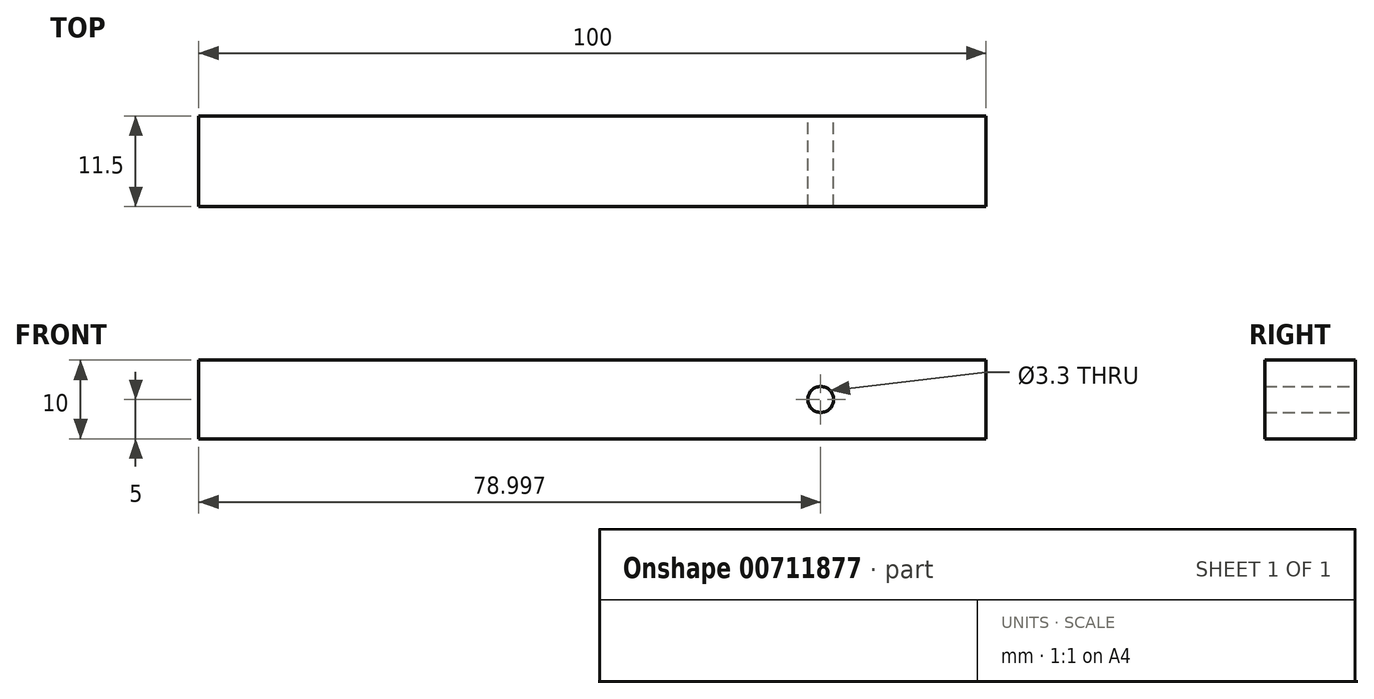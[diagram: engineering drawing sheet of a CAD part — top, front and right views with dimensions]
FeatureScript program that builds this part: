
annotation { "Feature Type Name" : "Feature", "Feature Type Description" : "" }
export const myFeature = defineFeature(function(context is Context, id is Id, definition is map)
    precondition{}
    {
        {
            var Q0;
            Q0=qCreatedBy(makeId("Top.planeOp"),FACE);
            var sketch = newSketch(context, id + "F0", { "sketchPlane" : qUnion([Q0])});
            skLineSegment(sketch, "E0.bottom", {"start": v(-19.05, 11.36) * mm, "end": v(80.95, 11.36) * mm});
            skLineSegment(sketch, "E0.top", {"start": v(-19.05, -0.14) * mm, "end": v(80.95, -0.14) * mm});
            skLineSegment(sketch, "E0.left", {"start": v(-19.05, 11.36) * mm, "end": v(-19.05, -0.14) * mm});
            skLineSegment(sketch, "E0.right", {"start": v(80.95, 11.36) * mm, "end": v(80.95, -0.14) * mm});
            skSolve(sketch);
        }
        {
            var Q0;
            Q0 = qSketchRegion(id + "F0", true);
            extrude(context, id + "F1", {"entities" : qUnion([Q0]), "depth" : 10 * mm, "offsetDistance" : 25 * mm});
        }
        {
            var Q0;
            Q0=makeQuery(id+"F1.opExtrude","SWEPT_FACE",FACE,{"disambiguationData":[OSD([sQuery(id+"F0.wireOp",EDGE,"E0.bottom")])]});
            var sketch = newSketch(context, id + "F2", { "sketchPlane" : qUnion([Q0])});
            skCircle(sketch, "E1", {"center": v(-59.95, 5) * mm, "radius": 1.65 * mm});
            skSolve(sketch);
        }
        {
            var Q0;
            Q0 = qSketchRegion(id + "F2", true);
            extrude(context, id + "F3", {"entities" : qUnion([Q0]), "operationType" : NewBodyOperationType.REMOVE, "oppositeDirection" : true, "depth" : 25 * mm, "offsetDistance" : 25 * mm});
        }
    });
